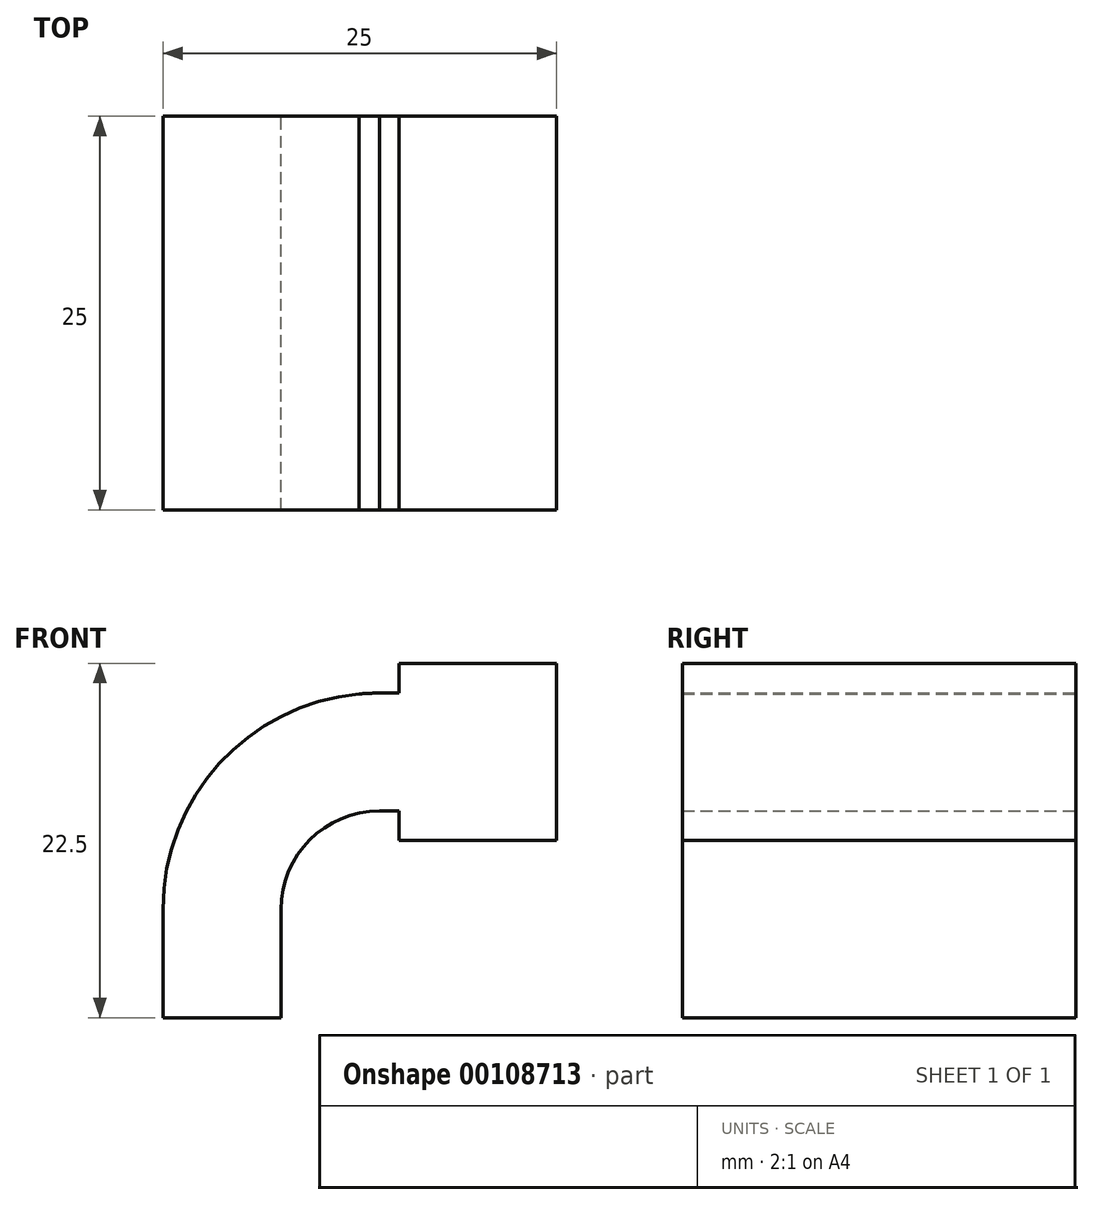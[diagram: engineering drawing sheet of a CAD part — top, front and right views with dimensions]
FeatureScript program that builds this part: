
annotation { "Feature Type Name" : "Feature", "Feature Type Description" : "" }
export const myFeature = defineFeature(function(context is Context, id is Id, definition is map)
    precondition{}
    {
        {
            var Q0;
            Q0=qCreatedBy(makeId("Front.planeOp"),FACE);
            var sketch = newSketch(context, id + "F0", { "sketchPlane" : qUnion([Q0])});
            skLineSegment(sketch, "E0.bottom", {"start": v(16.25, -3.75) * mm, "end": v(-16.25, -3.75) * mm});
            skLineSegment(sketch, "E0.top", {"start": v(16.25, 3.75) * mm, "end": v(-16.25, 3.75) * mm});
            skLineSegment(sketch, "E0.left", {"start": v(16.25, -3.75) * mm, "end": v(16.25, 3.75) * mm});
            skLineSegment(sketch, "E0.right", {"start": v(-16.25, -3.75) * mm, "end": v(-16.25, 3.75) * mm});
            skPoint(sketch, "E0.middle", {"position": v(0, 0) * mm});
            skLineSegment(sketch, "E1", {"start": v(16.25, 3.75) * mm, "end": v(16.25, 10.63) * mm});
            skLineSegment(sketch, "E2.bottom", {"start": v(43.75, 15) * mm, "end": v(23.75, 15) * mm});
            skLineSegment(sketch, "E2.top", {"start": v(43.75, 26.25) * mm, "end": v(23.75, 26.25) * mm});
            skLineSegment(sketch, "E2.left", {"start": v(43.75, 15) * mm, "end": v(43.75, 26.25) * mm});
            skLineSegment(sketch, "E2.right", {"start": v(23.75, 15) * mm, "end": v(23.75, 26.25) * mm});
            skPoint(sketch, "E2.middle", {"position": v(33.75, 20.62) * mm});
            skArc(sketch, "E3", {"start": v(16.25, 10.63) * mm, "mid": v(18.08, 15.05) * mm, "end": v(22.5, 16.88) * mm});
            skLineSegment(sketch, "E4", {"start": v(22.5, 16.88) * mm, "end": v(31.37, 16.88) * mm});
            skLineSegment(sketch, "E5.0", {"start": v(22.5, 24.38) * mm, "end": v(31.37, 24.38) * mm});
            skArc(sketch, "E5.1", {"start": v(8.75, 10.63) * mm, "mid": v(12.78, 20.35) * mm, "end": v(22.5, 24.38) * mm});
            skLineSegment(sketch, "E5.2", {"start": v(8.75, 3.75) * mm, "end": v(8.75, 10.63) * mm});
            skLineSegment(sketch, "E6", {"start": v(33.75, 15) * mm, "end": v(33.75, 26.25) * mm});
            skFitSpline(sketch, "E7", {"points": [v(-16.25, 3.75) * mm, v(22.5, 24.38) * mm], "startDerivative": vector(12.87, 48.02) * mm, "endDerivative": vector(48.03, 2) * mm});
            skSolve(sketch);
        }
        {
            var Q0;
            {var subQ7=sQuery(id+"F0.wireOp",EDGE,"E6");Q0=makeQuery(id+"F0.imprint","IMPRINT",FACE,{"disambiguationData":[TD([[makeQuery(id+"F0.imprint","IMPRINT",EDGE,{"derivedFrom":subQ7}),1.0]])]});}
            var Q1;
            {var subQ6=sQuery(id+"F0.wireOp",EDGE,"E1");Q1=makeQuery(id+"F0.imprint","IMPRINT",FACE,{"disambiguationData":[TD([[makeQuery(id+"F0.imprint","IMPRINT",EDGE,{"derivedFrom":subQ6}),1.0]])]});}
            extrude(context, id + "F1", {"entities" : qUnion([Q0, Q1]), "depth" : 25 * mm});
        }
    });
